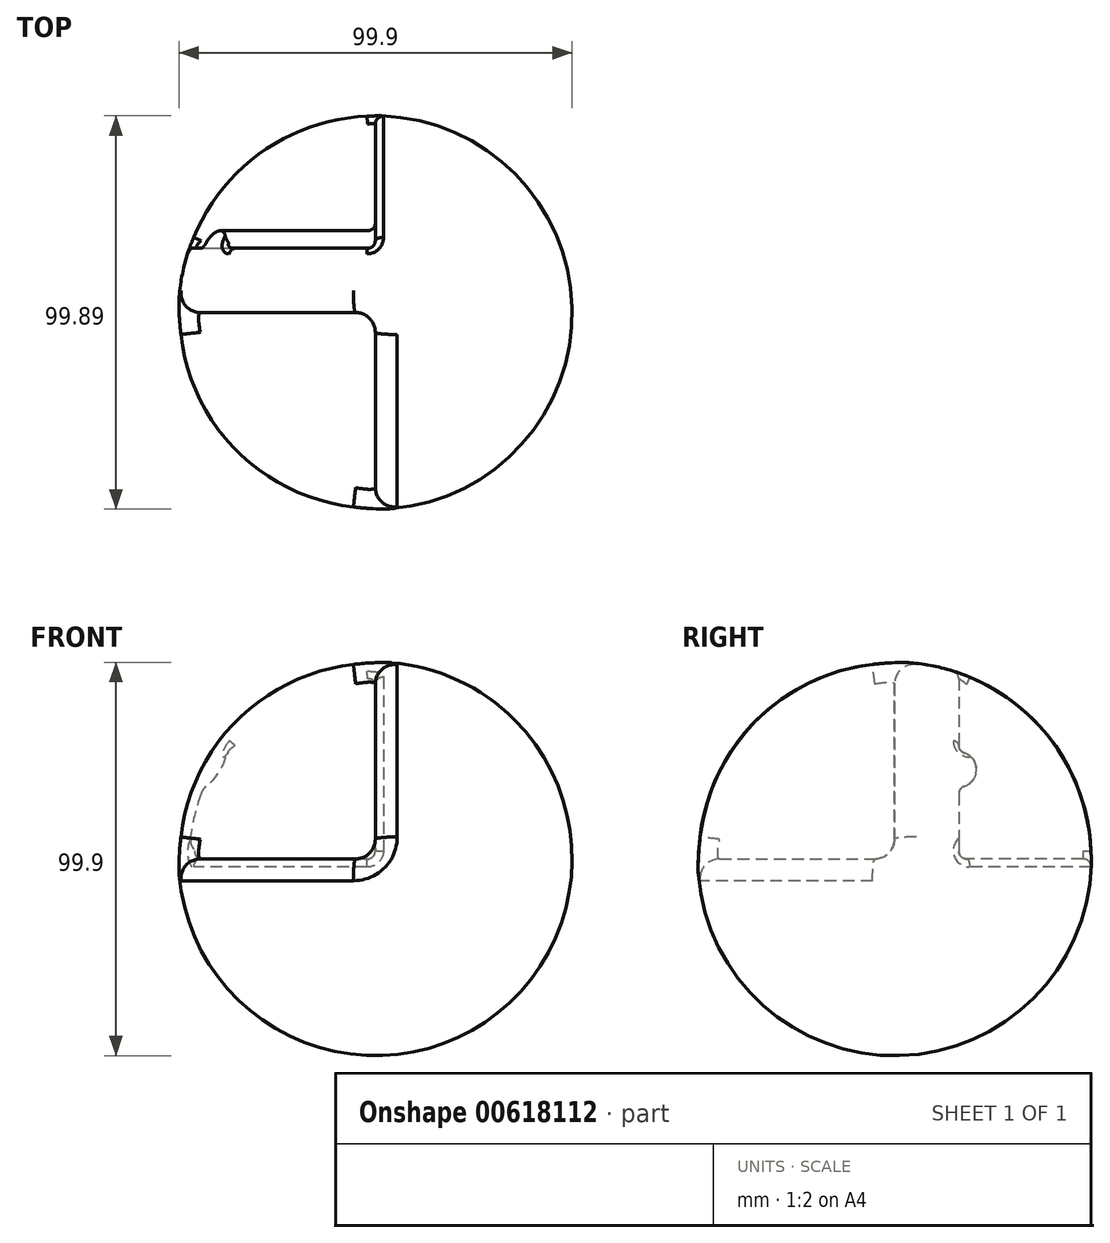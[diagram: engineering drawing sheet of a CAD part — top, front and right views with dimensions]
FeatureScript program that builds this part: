
annotation { "Feature Type Name" : "Feature", "Feature Type Description" : "" }
export const myFeature = defineFeature(function(context is Context, id is Id, definition is map)
    precondition{}
    {
        {
            var Q0;
            Q0=qCreatedBy(makeId("Top.planeOp"),FACE);
            var sketch = newSketch(context, id + "F0", { "sketchPlane" : qUnion([Q0])});
            skArc(sketch, "E0", {"start": v(0, 50) * mm, "mid": v(-50, 0) * mm, "end": v(0, -50) * mm});
            skLineSegment(sketch, "E1", {"start": v(0, 50) * mm, "end": v(0, -50) * mm});
            skSolve(sketch);
        }
        {
            var Q0;
            Q0=makeQuery(id+"F0.imprint","IMPRINT",FACE,{"disambiguationData":[TD([[makeQuery(id+"F0.imprint","IMPRINT",EDGE,{"derivedFrom":sQuery(id+"F0.wireOp",EDGE,"E0")}),1.0]])]});
            var Q1;
            Q1=sQuery(id+"F0.wireOp",EDGE,"E1");
            revolve(context, id + "F1", {"entities" : qUnion([Q0]), "axis" : qUnion([Q1]), "revolveType" : RevolveType.FULL});
        }
        {
            var Q0;
            Q0=qCreatedBy(makeId("Front.planeOp"),FACE);
            var sketch = newSketch(context, id + "F2", { "sketchPlane" : qUnion([Q0])});
            skLineSegment(sketch, "E2.bottom", {"start": v(0, 0) * mm, "end": v(-104.07, 0) * mm});
            skLineSegment(sketch, "E2.top", {"start": v(0, 117.6) * mm, "end": v(-104.07, 117.6) * mm});
            skLineSegment(sketch, "E2.left", {"start": v(0, 0) * mm, "end": v(0, 117.6) * mm});
            skLineSegment(sketch, "E2.right", {"start": v(-104.07, 0) * mm, "end": v(-104.07, 117.6) * mm});
            skSolve(sketch);
        }
        {
            var Q0;
            Q0=makeQuery(id+"F2.imprint","IMPRINT",FACE,{"disambiguationData":[TD([[makeQuery(id+"F2.imprint","IMPRINT",EDGE,{"derivedFrom":sQuery(id+"F2.wireOp",EDGE,"E2.bottom")}),-1.0]])]});
            extrude(context, id + "F3", {"entities" : qUnion([Q0]), "operationType" : NewBodyOperationType.REMOVE, "depth" : 87.8 * mm, "offsetDistance" : 25 * mm});
        }
        {
            var Q0;
            Q0=makeQuery(id+"F3.boolean.opBoolean","COPY",EDGE,{"derivedFrom":makeQuery(id+"F3.opExtrude","CAP_EDGE",EDGE,{"disambiguationData":[OSD([sQuery(id+"F2.wireOp",EDGE,"E2.left")])],"isStart":true})});
            var Q1;
            Q1=makeQuery(id+"F3.boolean.opBoolean","COPY",EDGE,{"derivedFrom":makeQuery(id+"F3.opExtrude","CAP_EDGE",EDGE,{"disambiguationData":[OSD([sQuery(id+"F2.wireOp",EDGE,"E2.bottom")])],"isStart":true})});
            var Q2;
            Q2=makeQuery(id+"F3.boolean.opBoolean","COPY",EDGE,{"derivedFrom":makeQuery(id+"F3.opExtrude","SWEPT_EDGE",EDGE,{"disambiguationData":[OSD([sQuery(id+"F2.wireOp",EDGE,"E2.bottom"),sQuery(id+"F2.wireOp",EDGE,"E2.left")])]})});
            fillet(context, id + "F4", {"entities" : qUnion([Q0, Q1, Q2]), "radius" : 5 * mm, "tangentPropagation" : true, "allowEdgeOverflow" : false});
        }
        {
            var Q0;
            Q0=makeQuery(id+"F3.boolean.opBoolean","INTERSECT",EDGE,{"derivedFrom":[makeQuery(id+"F1.opRevolve","SWEPT_FACE",FACE,{"disambiguationData":[OSD([sQuery(id+"F0.wireOp",EDGE,"E0")])]}),makeQuery(id+"F3.opExtrude","SWEPT_FACE",FACE,{"disambiguationData":[OSD([sQuery(id+"F2.wireOp",EDGE,"E2.left")])]})]});
            fillet(context, id + "F5", {"entities" : qUnion([Q0]), "radius" : 5 * mm, "tangentPropagation" : true, "allowEdgeOverflow" : false});
        }
        {
            var Q0;
            Q0=qCreatedBy(makeId("Right.planeOp"),FACE);
            var sketch = newSketch(context, id + "F6", { "sketchPlane" : qUnion([Q0])});
            skLineSegment(sketch, "E3.bottom", {"start": v(51.85, 70.62) * mm, "end": v(16.32, 70.62) * mm});
            skLineSegment(sketch, "E3.top", {"start": v(51.85, 0) * mm, "end": v(16.32, 0) * mm});
            skLineSegment(sketch, "E3.left", {"start": v(51.85, 70.62) * mm, "end": v(51.85, 0) * mm});
            skLineSegment(sketch, "E3.right", {"start": v(16.32, 70.62) * mm, "end": v(16.32, 27.13) * mm});
            skArc(sketch, "E4", {"start": v(16.32, 18.2) * mm, "mid": v(20.78, 22.66) * mm, "end": v(16.32, 27.13) * mm});
            skLineSegment(sketch, "E5.trimOffspring", {"start": v(16.32, 18.2) * mm, "end": v(16.32, 0) * mm});
            skSolve(sketch);
        }
        {
            var Q0;
            Q0 = qSketchRegion(id + "F6", true);
            var sketch = newSketch(context, id + "F7", { "sketchPlane" : qUnion([Q0])});
            skSolve(sketch);
        }
        {
            var Q0;
            Q0=makeQuery(id+"F7.imprint","IMPRINT",FACE,{"disambiguationData":[TD([[makeQuery(id+"F7.imprint","IMPRINT",EDGE,{"derivedFrom":makeQuery(id+"F6.imprint","IMPRINT",EDGE,{"derivedFrom":sQuery(id+"F6.wireOp",EDGE,"E3.bottom")})}),1.0]])]});
            extrude(context, id + "F8", {"entities" : qUnion([Q0]), "operationType" : NewBodyOperationType.REMOVE, "endBound" : BoundingType.THROUGH_ALL, "oppositeDirection" : true, "depth" : 25 * mm, "offsetDistance" : 25 * mm});
        }
        {
            var Q0;
            Q0=makeQuery(id+"F8.boolean.opBoolean","INTERSECT",EDGE,{"derivedFrom":[makeQuery(id+"F1.opRevolve","SWEPT_FACE",FACE,{"disambiguationData":[OSD([sQuery(id+"F0.wireOp",EDGE,"E0")])]}),makeQuery(id+"F8.opExtrude","CAP_FACE",FACE,{"disambiguationData":[OSD([sQuery(id+"F6.wireOp",EDGE,"E3.bottom"),sQuery(id+"F6.wireOp",EDGE,"E3.top"),sQuery(id+"F6.wireOp",EDGE,"E3.left"),sQuery(id+"F6.wireOp",EDGE,"E3.right")])],"isStart":true})]});
            var Q1;
            Q1=makeQuery(id+"F8.boolean.opBoolean","INTERSECT",EDGE,{"derivedFrom":[makeQuery(id+"F1.opRevolve","SWEPT_FACE",FACE,{"disambiguationData":[OSD([sQuery(id+"F0.wireOp",EDGE,"E0")])]}),makeQuery(id+"F8.opExtrude","SWEPT_FACE",FACE,{"disambiguationData":[OSD([sQuery(id+"F6.wireOp",EDGE,"E3.right")])]})]});
            var Q2;
            Q2=makeQuery(id+"F8.boolean.opBoolean","INTERSECT",EDGE,{"derivedFrom":[makeQuery(id+"F1.opRevolve","SWEPT_FACE",FACE,{"disambiguationData":[OSD([sQuery(id+"F0.wireOp",EDGE,"E0")])]}),makeQuery(id+"F8.opExtrude","SWEPT_FACE",FACE,{"disambiguationData":[OSD([sQuery(id+"F6.wireOp",EDGE,"E3.top")])]})]});
            var Q3;
            Q3=makeQuery(id+"F8.boolean.opBoolean","COPY",FACE,{"derivedFrom":makeQuery(id+"F8.opExtrude","SWEPT_FACE",FACE,{"disambiguationData":[OSD([sQuery(id+"F6.wireOp",EDGE,"E3.right")])]})});
            var Q4;
            Q4=makeQuery(id+"F8.boolean.opBoolean","COPY",EDGE,{"derivedFrom":makeQuery(id+"F8.opExtrude","CAP_EDGE",EDGE,{"disambiguationData":[OSD([sQuery(id+"F6.wireOp",EDGE,"E3.top")])],"isStart":true})});
            var Q5;
            Q5=makeQuery(id+"F8.boolean.opBoolean","COPY",EDGE,{"derivedFrom":makeQuery(id+"F8.opExtrude","CAP_EDGE",EDGE,{"disambiguationData":[OSD([sQuery(id+"F6.wireOp",EDGE,"E4")])],"isStart":true})});
            var Q6;
            Q6=makeQuery(id+"F8.boolean.opBoolean","COPY",EDGE,{"derivedFrom":makeQuery(id+"F8.opExtrude","SWEPT_EDGE",EDGE,{"disambiguationData":[OSD([sQuery(id+"F6.wireOp",EDGE,"E4"),sQuery(id+"F6.wireOp",EDGE,"E5.trimOffspring")])]})});
            var Q7;
            Q7=makeQuery(id+"F8.boolean.opBoolean","COPY",EDGE,{"derivedFrom":makeQuery(id+"F8.opExtrude","CAP_EDGE",EDGE,{"disambiguationData":[OSD([sQuery(id+"F6.wireOp",EDGE,"E5.trimOffspring")])],"isStart":true})});
            var Q8;
            Q8=makeQuery(id+"F8.boolean.opBoolean","COPY",EDGE,{"derivedFrom":makeQuery(id+"F8.opExtrude","SWEPT_EDGE",EDGE,{"disambiguationData":[OSD([sQuery(id+"F6.wireOp",EDGE,"E3.top"),sQuery(id+"F6.wireOp",EDGE,"E5.trimOffspring")])]})});
            fillet(context, id + "F9", {"entities" : qUnion([Q0, Q1, Q2, Q3, Q4, Q5, Q6, Q7, Q8]), "radius" : 2 * mm, "tangentPropagation" : true, "allowEdgeOverflow" : false});
        }
    });
